# Revit family: 05121_KRMM
name_source: partatom
category: Air Terminals
revit_build: Autodesk Revit MEP 2012 (Build: 20110309_2315(x64)
units: mm (PartAtom-declared; Revit-internal decimal feet)

## types (8) — shared parameters
Cuello Mín-Máx. = 6 a 20" en incrementos de 2".
Description = Difusor de Largo alcance
Función = Inyección
Manufacturer = INNES
Material = Aluminio
Model = KRMM
Nota1 = .
Posición de Instalación = Muro/Techo
Tipo de Cuello = Redondo
Type Comments = Tipo tobera
URL = https://www.innes.com.mx
Visible_Texto = No

## per-type parameters (varying)
| type | Conect | Medida_Requerida | Var1 | VarA |
| Diámetro 06" | 3 1/8" | 6" | 6 | 6 1/4" |
| Diámetro 08" | 4 1/8" | 8" | 8 | 8 1/4" |
| Diámetro 10" | 5 1/8" | 10" | 10 | 10 1/4" |
| Diámetro 12" | 6 1/8" | 12" | 12 | 12 1/4" |
| Diámetro 14" | 6 1/8" | 14" | 14 | 12 1/4" |
| Diámetro 16" | 8 1/8" | 16" | 16 | 16 1/4" |
| Diametro 18" | 10 1/8" | 18" | 18 | 20 1/4" |
| Diámetro 20" | 10 1/8" | 20" | 20 | 20 1/4" |

## geometry (parser evidence)
native form markers: Sweep x7
no freeform markers — native parametric forms only
